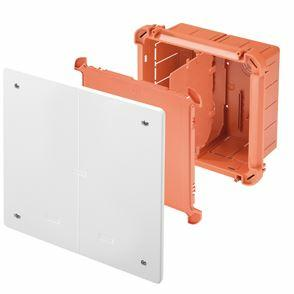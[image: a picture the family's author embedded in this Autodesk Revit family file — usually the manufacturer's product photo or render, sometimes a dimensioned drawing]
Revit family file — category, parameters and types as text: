
# Revit family: Building-ContenitoriIncasso-GEWISS-48CM-CASSETTE-DERIVAZIONE_INCASSO_GRANDE_CAPACITA
name_source: partatom
category: Apparecchi elettrici
revit_build: Autodesk Revit 2016 (Build: 20161004_0715(x64)
units: mm (PartAtom-declared; Revit-internal decimal feet)

## family parameters
Condiviso = No
Host = Superficie
Mantenere orientamento annotazione = Sì
Numero OmniClass = 23.80.30.14.24
Punto di calcolo locali = Sì
Quota connettore circolare = Usa diametro
Taglio con vuoti quando caricato = No
Tipo di parte = Normale
Titolo OmniClass = Junction Boxes

## types (2) — shared parameters
Bordo = 4 mm  [stored 0.0131234 ft]
Carico apparente = 0 VA
Catalogo = BUILDING
Catalogo Serie = 48 CM
Classificazione = Other
Codice Electrocod = 0220
Colore coperchio = Bianco RAL 9016
GEWISS SCHEDA TECNICA = http://pro.gewiss.com
Glow Wire Test = 650°C
Grado di protezione = IP40
IDF = ed542da5-95cd-4286-b3ab-eec61fb23eb6
IDT = 14496fa0-f6cd-4977-b717-7ad3c308566f
Immagine tipo = 48CM.JPG
Installazione = Incasso
Larghezza = 260 mm  [stored 0.853018 ft]
Lunghezza = 520 mm  [stored 1.70604 ft]
Per Pareti = Muratura
Produttore = GEWISS S.p.A.
Profondità = 121 mm  [stored 0.396982 ft]
Prospetto di default = 1219 mm
Resistenza agli urti = IK07
SEO = Cassetta
Scatola = ROSSO RAL 3000
Scheda Tecnica = https://www.gewiss.com
Tappo = GEWISS - BIANCO RAL 9016
Temperatura di impiego = -15 +60 °C
Termopressione con biglia = 70 °C
Tipo Materiale = Halogen free secondo norma EN 60754-2
URL = https://www.gewiss.com
Versione file RFA = 18.0
Voltaggio = 0 V

## per-type parameters (varying)
| type | Codice EAN | Descrizione | Dim. esterne BxHxP (mm) | Modello | Potenza dissipabile (W) | Potenza max dissipabile (W) | Predisposizione scomparti |
| GW48211 - CASSETTA MONTANTI 520X260X121 COP.BASSO | 8011564027299 | CASSETTA MONTANTI 520X260X121 COP.BASSO | 520x260x121 | GW48211 | 30 | 30 | 5 |
| GW48207 - CASSETTA MONTANTI 260X260X121 COP.BASSO | 8011564027282 | CASSETTA MONTANTI 260X260X121 COP.BASSO | 260x260x121 | GW48207 | 13 | 13 | 2 |

note: [stored X ft] marks values corroborated as IEEE doubles in the binary element streams (Revit-internal decimal feet)

## geometry (parser evidence)
native form markers: Blend x2, Sweep x1
no freeform markers — native parametric forms only
